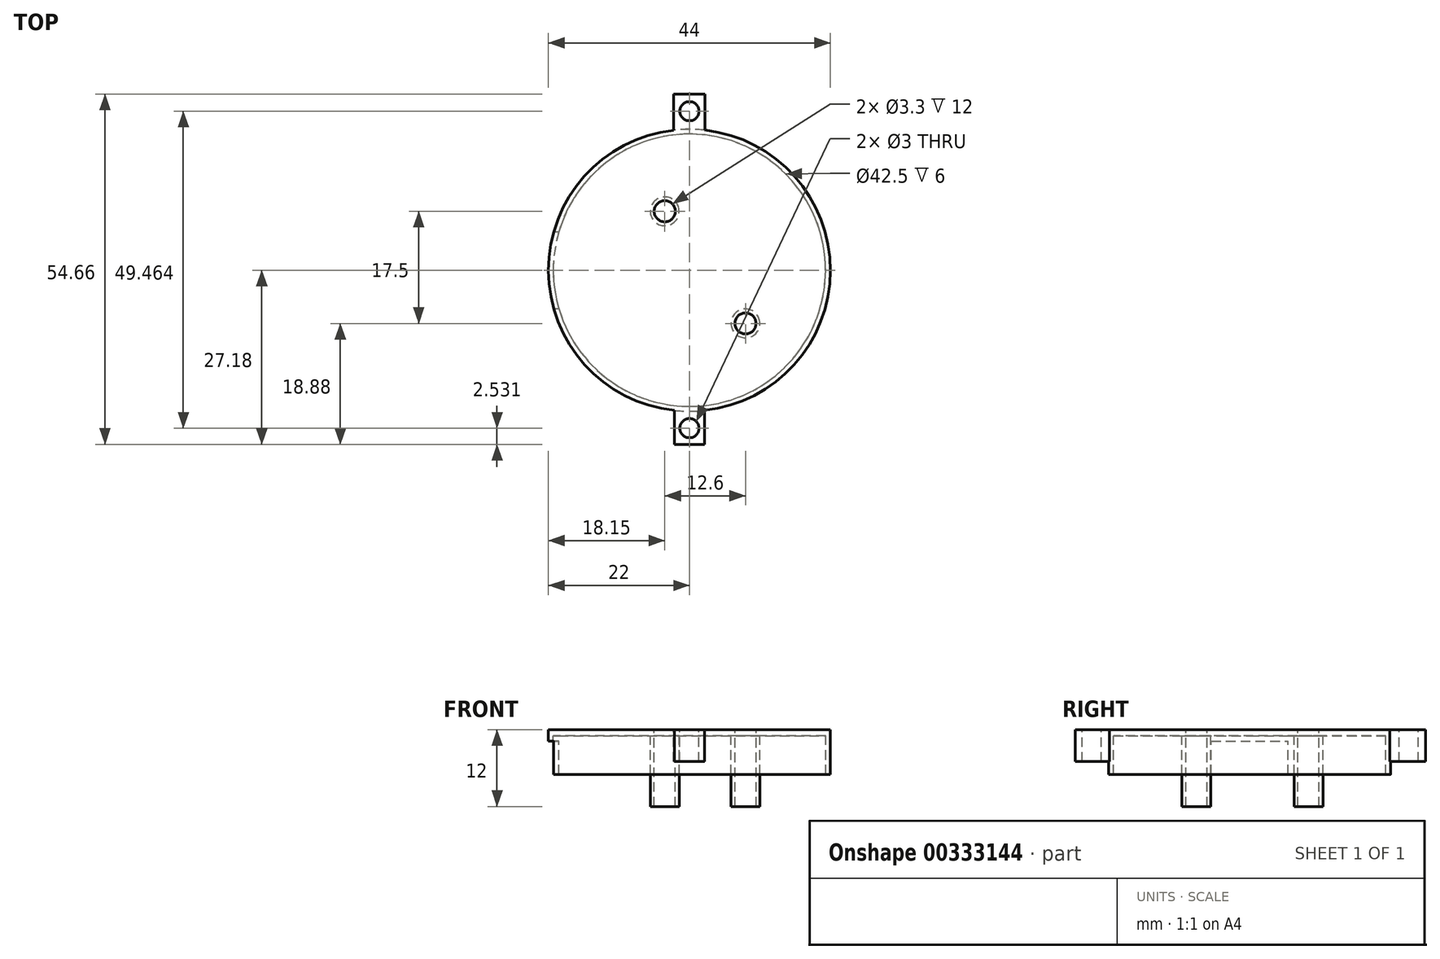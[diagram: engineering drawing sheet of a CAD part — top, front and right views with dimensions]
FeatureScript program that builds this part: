
annotation { "Feature Type Name" : "Feature", "Feature Type Description" : "" }
export const myFeature = defineFeature(function(context is Context, id is Id, definition is map)
    precondition{}
    {
        {
            var Q0;
            Q0=qCreatedBy(makeId("Top.planeOp"),FACE);
            var sketch = newSketch(context, id + "F0", { "sketchPlane" : qUnion([Q0])});
            skLineSegment(sketch, "E0.bottom", {"start": v(11.95, -11.5) * mm, "end": v(-11.95, -11.5) * mm});
            skLineSegment(sketch, "E0.top", {"start": v(11.95, 11.5) * mm, "end": v(-11.95, 11.5) * mm});
            skLineSegment(sketch, "E0.left", {"start": v(11.95, -11.5) * mm, "end": v(11.95, 11.5) * mm});
            skLineSegment(sketch, "E0.right", {"start": v(-11.95, -11.5) * mm, "end": v(-11.95, 11.5) * mm});
            skPoint(sketch, "E0.middle", {"position": v(0, 0) * mm});
            skCircle(sketch, "E1", {"center": v(0, 0) * mm, "radius": 22 * mm});
            skCircle(sketch, "E2", {"center": v(8.75, -8.3) * mm, "radius": 1.65 * mm});
            skCircle(sketch, "E3", {"center": v(-3.85, 9.2) * mm, "radius": 2.25 * mm});
            skCircle(sketch, "E4", {"center": v(0, 24.81) * mm, "radius": 1.5 * mm});
            skLineSegment(sketch, "E5", {"start": v(2.42, 21.87) * mm, "end": v(2.42, 27.48) * mm});
            skLineSegment(sketch, "E6", {"start": v(-2.46, 21.86) * mm, "end": v(-2.46, 27.48) * mm});
            skLineSegment(sketch, "E7", {"start": v(-2.46, 27.48) * mm, "end": v(2.42, 27.48) * mm});
            skCircle(sketch, "E8", {"center": v(0, -24.65) * mm, "radius": 1.5 * mm});
            skLineSegment(sketch, "E9", {"start": v(-2.34, -21.87) * mm, "end": v(-2.34, -27.18) * mm});
            skLineSegment(sketch, "E10", {"start": v(2.33, -21.88) * mm, "end": v(2.33, -27.18) * mm});
            skLineSegment(sketch, "E11", {"start": v(2.33, -27.18) * mm, "end": v(-2.34, -27.18) * mm});
            skCircle(sketch, "E12", {"center": v(-3.85, 9.2) * mm, "radius": 1.65 * mm});
            skCircle(sketch, "E13", {"center": v(8.75, -8.3) * mm, "radius": 2.25 * mm});
            skSolve(sketch);
        }
        {
            var Q0;
            Q0=makeQuery(id+"F0.imprint","IMPRINT",FACE,{"disambiguationData":[TD([[makeQuery(id+"F0.imprint","IMPRINT",EDGE,{"derivedFrom":sQuery(id+"F0.wireOp",EDGE,"E0.bottom")}),1.0]])]});
            extrude(context, id + "F1", {"entities" : qUnion([Q0]), "oppositeDirection" : true, "depth" : 7 * mm});
        }
        {
            var Q0;
            Q0=makeQuery(id+"F0.imprint","IMPRINT",FACE,{"disambiguationData":[TD([[makeQuery(id+"F0.imprint","IMPRINT",EDGE,{"derivedFrom":sQuery(id+"F0.wireOp",EDGE,"E0.bottom")}),-1.0]])]});
            extrude(context, id + "F2", {"entities" : qUnion([Q0]), "operationType" : NewBodyOperationType.ADD, "oppositeDirection" : true, "depth" : 1 * mm});
        }
        {
            var Q0;
            Q0=makeQuery(id+"F1.opExtrude","SWEPT_FACE",FACE,{"disambiguationData":[OSD([sQuery(id+"F0.wireOp",EDGE,"E0.right")])]});
            var sketch = newSketch(context, id + "F3", { "sketchPlane" : qUnion([Q0])});
            skLineSegment(sketch, "E14.bottom", {"start": v(-6, -1.8) * mm, "end": v(6, -1.8) * mm});
            skLineSegment(sketch, "E14.top", {"start": v(-6, -7.8) * mm, "end": v(6, -7.8) * mm});
            skLineSegment(sketch, "E14.left", {"start": v(-6, -1.8) * mm, "end": v(-6, -7.8) * mm});
            skLineSegment(sketch, "E14.right", {"start": v(6, -1.8) * mm, "end": v(6, -7.8) * mm});
            skPoint(sketch, "E14.middle", {"position": v(0, -4.8) * mm});
            skSolve(sketch);
        }
        {
            var Q0;
            Q0 = qSketchRegion(id + "F3", true);
            extrude(context, id + "F4", {"entities" : qUnion([Q0]), "operationType" : NewBodyOperationType.REMOVE, "oppositeDirection" : true, "depth" : 25 * mm});
        }
        {
            var Q0;
            Q0=makeQuery(id+"F2.opExtrude","CAP_FACE",FACE,{"disambiguationData":[OSD([sQuery(id+"F0.wireOp",EDGE,"E0.bottom"),sQuery(id+"F0.wireOp",EDGE,"E0.top"),sQuery(id+"F0.wireOp",EDGE,"E0.left"),sQuery(id+"F0.wireOp",EDGE,"E0.right"),sQuery(id+"F0.wireOp",EDGE,"E2"),sQuery(id+"F0.wireOp",EDGE,"E3")])],"isStart":false});
            var sketch = newSketch(context, id + "F5", { "sketchPlane" : qUnion([Q0])});
            skCircle(sketch, "E15", {"center": v(0, 0) * mm, "radius": 21.25 * mm});
            skSolve(sketch);
        }
        {
            var Q0;
            Q0 = qSketchRegion(id + "F5", true);
            var Q1;
            Q1=makeQuery(id+"FFNihRlScpWBl9j_1.opExtrude","CAP_FACE",FACE,{"disambiguationData":[OSD([sQuery(id+"F0.wireOp",EDGE,"E3")])],"isStart":false});
            var Q2;
            Q2=makeQuery(id+"FFNihRlScpWBl9j_1.opExtrude","CAP_FACE",FACE,{"disambiguationData":[OSD([sQuery(id+"F0.wireOp",EDGE,"E2")])],"isStart":false});
            extrude(context, id + "F6", {"entities" : qUnion([Q0, Q1, Q2]), "operationType" : NewBodyOperationType.REMOVE, "depth" : 10 * mm});
        }
        {
            var Q0;
            Q0=makeQuery(id+"F0.imprint","IMPRINT",FACE,{"disambiguationData":[TD([[makeQuery(id+"F0.imprint","IMPRINT",EDGE,{"derivedFrom":sQuery(id+"F0.wireOp",EDGE,"E3")}),1.0]])]});
            var Q1;
            Q1=makeQuery(id+"F0.imprint","IMPRINT",FACE,{"disambiguationData":[TD([[makeQuery(id+"F0.imprint","IMPRINT",EDGE,{"derivedFrom":sQuery(id+"F0.wireOp",EDGE,"E2")}),-1.0]])]});
            extrude(context, id + "F7", {"entities" : qUnion([Q0, Q1]), "operationType" : NewBodyOperationType.ADD, "oppositeDirection" : true, "depth" : 12 * mm});
        }
        {
            var Q0;
            Q0=makeQuery(id+"F0.imprint","IMPRINT",FACE,{"disambiguationData":[TD([[makeQuery(id+"F0.imprint","IMPRINT",EDGE,{"derivedFrom":sQuery(id+"F0.wireOp",EDGE,"E4")}),-1.0]])]});
            var Q1;
            Q1=makeQuery(id+"F0.imprint","IMPRINT",FACE,{"disambiguationData":[TD([[makeQuery(id+"F0.imprint","IMPRINT",EDGE,{"derivedFrom":sQuery(id+"F0.wireOp",EDGE,"E8")}),-1.0]])]});
            extrude(context, id + "F8", {"entities" : qUnion([Q0, Q1]), "operationType" : NewBodyOperationType.ADD, "oppositeDirection" : true, "depth" : 5 * mm});
        }
    });
